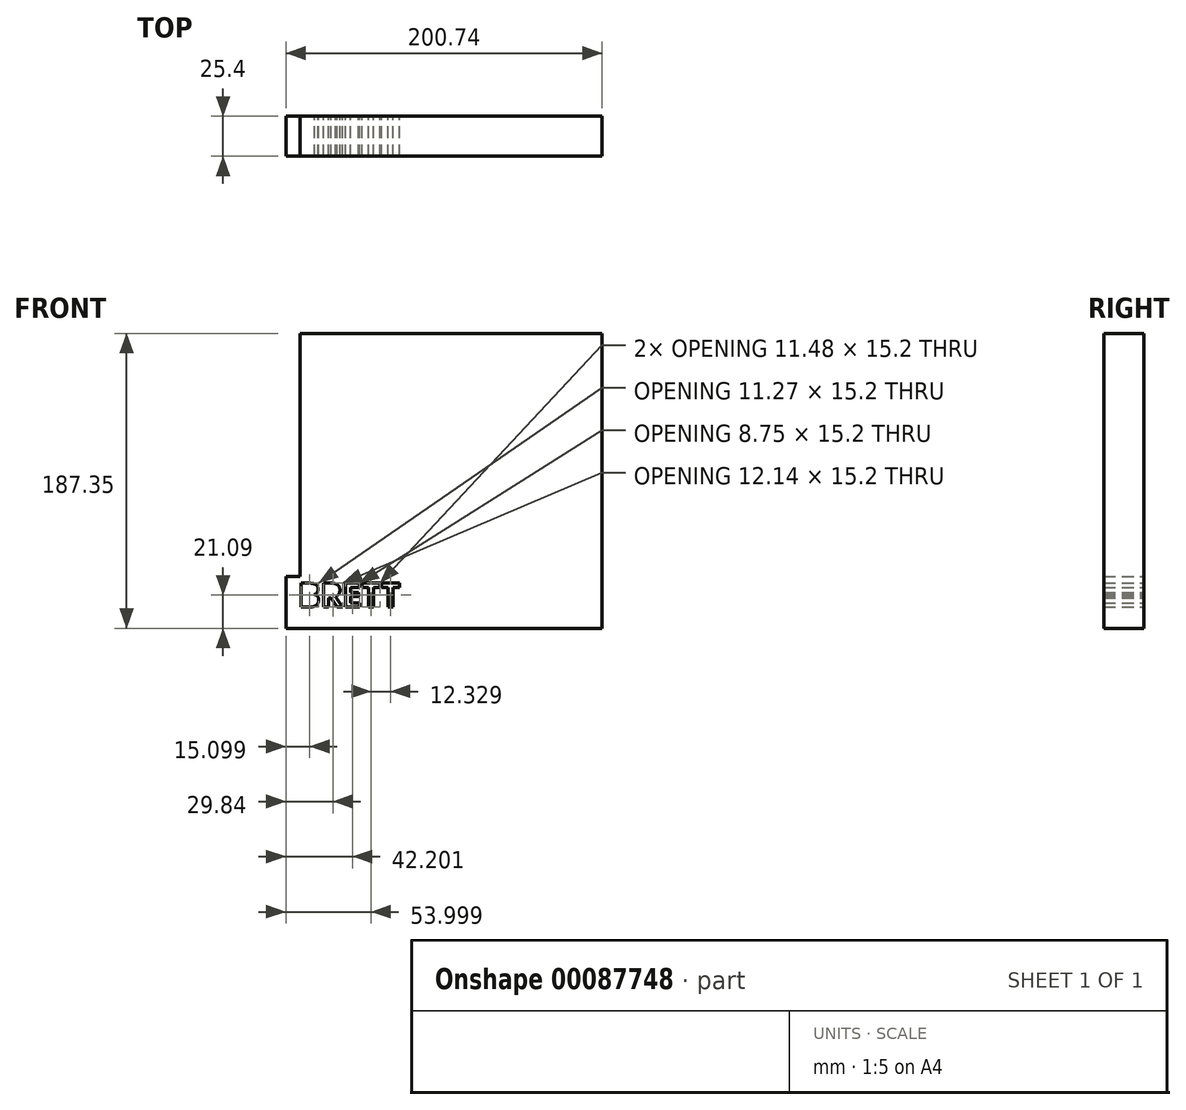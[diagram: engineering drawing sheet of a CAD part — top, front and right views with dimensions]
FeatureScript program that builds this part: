
annotation { "Feature Type Name" : "Feature", "Feature Type Description" : "" }
export const myFeature = defineFeature(function(context is Context, id is Id, definition is map)
    precondition{}
    {
        {
            var Q0;
            Q0=qCreatedBy(makeId("Front.planeOp"),FACE);
            var sketch = newSketch(context, id + "F0", { "sketchPlane" : qUnion([Q0])});
            skFitSpline(sketch, "E0", {"points": [v(-229.65, -59.8) * mm, v(-194.87, 7.24) * mm, v(-210.37, -7.72) * mm], "startDerivative": vector(85.27, 150.35) * mm, "endDerivative": vector(-61.58, -68.33) * mm});
            skLineSegment(sketch, "E1.bottom", {"start": v(-168.05, -97.75) * mm, "end": v(32.69, -97.75) * mm});
            skLineSegment(sketch, "E1.top", {"start": v(-168.05, -64.95) * mm, "end": v(32.69, -64.95) * mm});
            skLineSegment(sketch, "E1.left", {"start": v(-168.05, -97.75) * mm, "end": v(-168.05, -64.95) * mm});
            skLineSegment(sketch, "E1.right", {"start": v(32.69, -97.75) * mm, "end": v(32.69, -64.95) * mm});
            skLineSegment(sketch, "E2.bottom", {"start": v(32.69, -64.95) * mm, "end": v(-159.25, -64.95) * mm});
            skLineSegment(sketch, "E2.top", {"start": v(32.69, 89.6) * mm, "end": v(-159.25, 89.6) * mm});
            skLineSegment(sketch, "E2.left", {"start": v(32.69, -64.95) * mm, "end": v(32.69, 89.6) * mm});
            skLineSegment(sketch, "E2.right", {"start": v(-159.25, -64.95) * mm, "end": v(-159.25, 89.6) * mm});
            skText(sketch, "E3", { "text": "BRETT", "fontName": "OpenSans-Bold.ttf"});
            const initialGuessF0  = {"E3": [-0.1605, -0.08426, 1, 0, 0.01533]};
            skSetInitialGuess(sketch, initialGuessF0);
            skSolve(sketch);
        }
        {
            var Q0;
            Q0 = qSketchRegion(id + "F0", true);
            extrude(context, id + "F1", {"entities" : qUnion([Q0]), "endBound" : BoundingType.SYMMETRIC, "depth" : 25.4 * mm});
        }
    });
